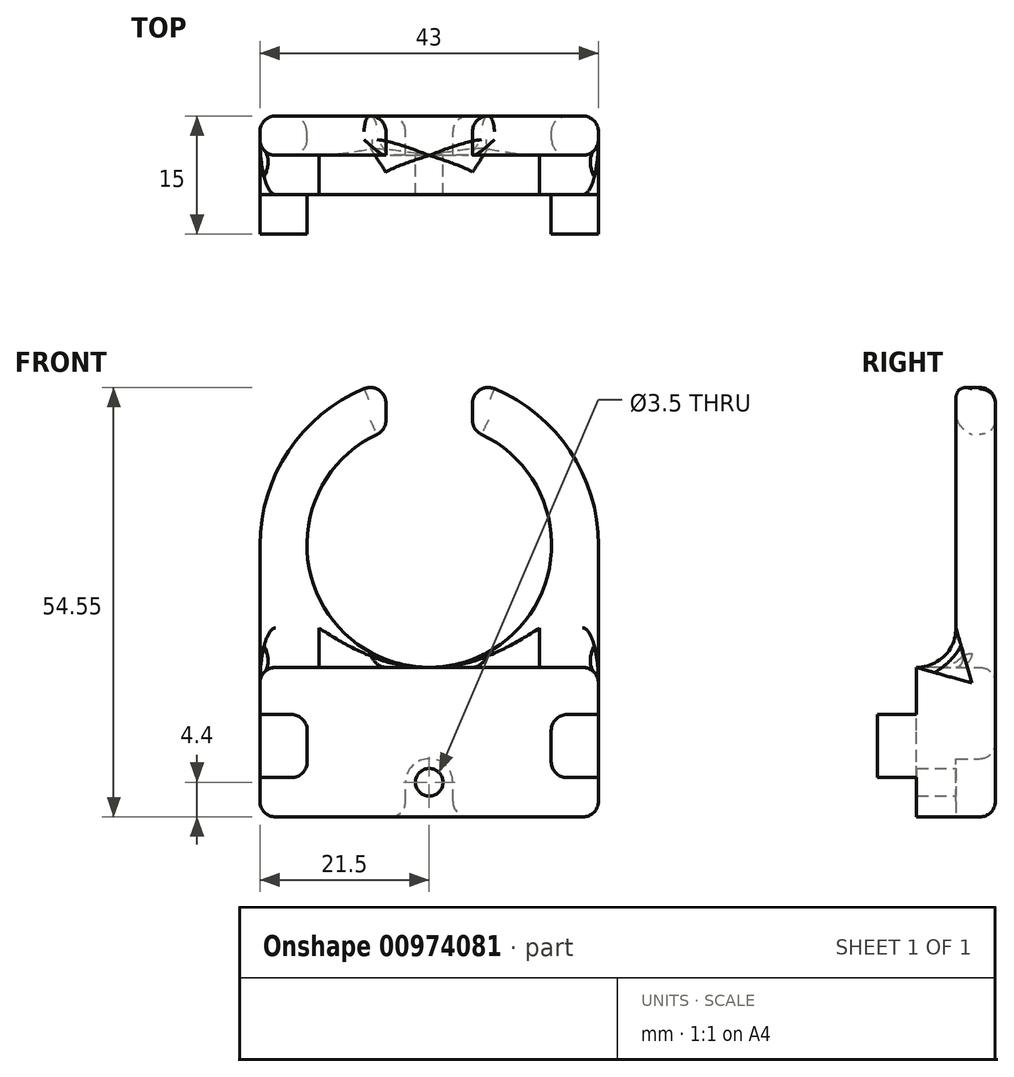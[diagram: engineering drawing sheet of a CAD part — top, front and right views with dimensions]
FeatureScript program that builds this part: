
annotation { "Feature Type Name" : "Feature", "Feature Type Description" : "" }
export const myFeature = defineFeature(function(context is Context, id is Id, definition is map)
    precondition{}
    {
        {
            var Q0;
            Q0=qCreatedBy(makeId("Front.planeOp"),FACE);
            var sketch = newSketch(context, id + "F0", { "sketchPlane" : qUnion([Q0])});
            skLineSegment(sketch, "E0.bottom", {"start": v(0, 0) * mm, "end": v(-43, 0) * mm});
            skLineSegment(sketch, "E0.top", {"start": v(0, 19) * mm, "end": v(-43, 19) * mm, "construction": true});
            skLineSegment(sketch, "E0.left", {"start": v(0, 0) * mm, "end": v(0, 19) * mm});
            skLineSegment(sketch, "E0.right", {"start": v(-43, 0) * mm, "end": v(-43, 19) * mm});
            skArc(sketch, "E1", {"start": v(0, 34.55) * mm, "mid": v(-21.5, 56.05) * mm, "end": v(-43, 34.55) * mm});
            skCircle(sketch, "E2", {"center": v(-21.5, 34.55) * mm, "radius": 15.55 * mm});
            skLineSegment(sketch, "E3", {"start": v(-43, 19) * mm, "end": v(-43, 34.55) * mm});
            skLineSegment(sketch, "E4", {"start": v(0, 19) * mm, "end": v(0, 34.55) * mm});
            skSolve(sketch);
        }
        {
            var Q0;
            Q0 = qSketchRegion(id + "F0", true);
            extrude(context, id + "F1", {"entities" : qUnion([Q0]), "depth" : 5 * mm, "offsetDistance" : 25 * mm});
        }
        {
            var Q0;
            Q0=makeQuery(id+"F1.opExtrude","CAP_FACE",FACE,{"disambiguationData":[OSD([sQuery(id+"F0.wireOp",EDGE,"E0.bottom"),sQuery(id+"F0.wireOp",EDGE,"E0.left"),sQuery(id+"F0.wireOp",EDGE,"E0.right"),sQuery(id+"F0.wireOp",EDGE,"E1"),sQuery(id+"F0.wireOp",EDGE,"E2"),sQuery(id+"F0.wireOp",EDGE,"E3"),sQuery(id+"F0.wireOp",EDGE,"E4")])],"isStart":false});
            var sketch = newSketch(context, id + "F2", { "sketchPlane" : qUnion([Q0])});
            skLineSegment(sketch, "E5.bottom", {"start": v(0, 0) * mm, "end": v(-43, 0) * mm});
            skLineSegment(sketch, "E5.top", {"start": v(0, 19) * mm, "end": v(-43, 19) * mm});
            skLineSegment(sketch, "E5.left", {"start": v(0, 0) * mm, "end": v(0, 19) * mm});
            skLineSegment(sketch, "E5.right", {"start": v(-43, 0) * mm, "end": v(-43, 19) * mm});
            skSolve(sketch);
        }
        {
            var Q0;
            {var subQ0=makeQuery(id+"F1.opExtrude","CAP_EDGE",EDGE,{"disambiguationData":[OSD([sQuery(id+"F0.wireOp",EDGE,"E1")])],"isStart":false});Q0=makeQuery(id+"F2.imprint","IMPRINT",FACE,{"disambiguationData":[TD([[makeQuery(id+"F2.imprint","IMPRINT",EDGE,{"derivedFrom":subQ0}),1.0]])]});}
            var sketch = newSketch(context, id + "F3", { "sketchPlane" : qUnion([Q0])});
            skLineSegment(sketch, "E6", {"start": v(-21.5, 34.05) * mm, "end": v(-21.5, 59.05) * mm, "construction": true});
            skLineSegment(sketch, "E7.bottom", {"start": v(-27, 59.05) * mm, "end": v(-16, 59.05) * mm});
            skLineSegment(sketch, "E7.top", {"start": v(-27, 47.05) * mm, "end": v(-16, 47.05) * mm});
            skLineSegment(sketch, "E7.left", {"start": v(-27, 59.05) * mm, "end": v(-27, 47.05) * mm});
            skLineSegment(sketch, "E7.right", {"start": v(-16, 59.05) * mm, "end": v(-16, 47.05) * mm});
            skSolve(sketch);
        }
        {
            var Q0;
            Q0 = qSketchRegion(id + "F3", true);
            var Q1;
            Q1=makeQuery(id+"F1.opExtrude","CAP_FACE",FACE,{"disambiguationData":[OSD([sQuery(id+"F0.wireOp",EDGE,"E0.bottom"),sQuery(id+"F0.wireOp",EDGE,"E0.left"),sQuery(id+"F0.wireOp",EDGE,"E0.right"),sQuery(id+"F0.wireOp",EDGE,"E1"),sQuery(id+"F0.wireOp",EDGE,"E2"),sQuery(id+"F0.wireOp",EDGE,"E3"),sQuery(id+"F0.wireOp",EDGE,"E4")])],"isStart":true});
            extrude(context, id + "F4", {"entities" : qUnion([Q0]), "operationType" : NewBodyOperationType.REMOVE, "endBound" : BoundingType.UP_TO_SURFACE, "oppositeDirection" : true, "depth" : 25 * mm, "endBoundEntityFace" : qUnion([Q1]), "offsetDistance" : 25 * mm});
        }
        {
            var Q0;
            Q0 = qSketchRegion(id + "F2", true);
            extrude(context, id + "F5", {"entities" : qUnion([Q0]), "operationType" : NewBodyOperationType.ADD, "depth" : 5 * mm, "offsetDistance" : 25 * mm});
        }
        {
            var Q0;
            Q0=makeQuery(id+"F5.opExtrude","CAP_FACE",FACE,{"disambiguationData":[OSD([sQuery(id+"F2.wireOp",EDGE,"E5.bottom"),sQuery(id+"F2.wireOp",EDGE,"E5.top"),sQuery(id+"F2.wireOp",EDGE,"E5.left"),sQuery(id+"F2.wireOp",EDGE,"E5.right")])],"isStart":false});
            var sketch = newSketch(context, id + "F6", { "sketchPlane" : qUnion([Q0])});
            skLineSegment(sketch, "E8.bottom", {"start": v(-43, 5) * mm, "end": v(-37, 5) * mm});
            skLineSegment(sketch, "E8.top", {"start": v(-43, 13) * mm, "end": v(-37, 13) * mm});
            skLineSegment(sketch, "E8.left", {"start": v(-43, 5) * mm, "end": v(-43, 13) * mm});
            skLineSegment(sketch, "E8.right", {"start": v(-37, 5) * mm, "end": v(-37, 13) * mm});
            skLineSegment(sketch, "E9.bottom", {"start": v(0, 13) * mm, "end": v(-6, 13) * mm});
            skLineSegment(sketch, "E9.top", {"start": v(0, 5) * mm, "end": v(-6, 5) * mm});
            skLineSegment(sketch, "E9.left", {"start": v(0, 13) * mm, "end": v(0, 5) * mm});
            skLineSegment(sketch, "E9.right", {"start": v(-6, 13) * mm, "end": v(-6, 5) * mm});
            skSolve(sketch);
        }
        {
            var Q0;
            Q0 = qSketchRegion(id + "F6", true);
            extrude(context, id + "F7", {"entities" : qUnion([Q0]), "operationType" : NewBodyOperationType.ADD, "depth" : 5 * mm, "offsetDistance" : 25 * mm});
        }
        {
            var Q0;
            Q0=makeQuery(id+"F1.opExtrude","CAP_EDGE",EDGE,{"disambiguationData":[OSD([sQuery(id+"F0.wireOp",EDGE,"E0.left"),sQuery(id+"F0.wireOp",EDGE,"E4")])],"isStart":false});
            var Q1;
            Q1=makeQuery(id+"F1.opExtrude","CAP_EDGE",EDGE,{"disambiguationData":[OSD([sQuery(id+"F0.wireOp",EDGE,"E2")])],"isStart":false});
            var Q2;
            Q2=makeQuery(id+"F1.opExtrude","CAP_EDGE",EDGE,{"disambiguationData":[OSD([sQuery(id+"F0.wireOp",EDGE,"E2")])],"isStart":true});
            var Q3;
            Q3=makeQuery(id+"F1.opExtrude","CAP_EDGE",EDGE,{"disambiguationData":[OSD([sQuery(id+"F0.wireOp",EDGE,"E0.left"),sQuery(id+"F0.wireOp",EDGE,"E4")])],"isStart":true});
            var Q4;
            Q4=makeQuery(id+"F1.opExtrude","CAP_EDGE",EDGE,{"disambiguationData":[OSD([sQuery(id+"F0.wireOp",EDGE,"E0.bottom")])],"isStart":true});
            var Q5;
            Q5=makeQuery(id+"F5.boolean.opBoolean","MERGE",EDGE,{"derivedFrom":[makeQuery(id+"F1.opExtrude","SWEPT_EDGE",EDGE,{"disambiguationData":[OSD([sQuery(id+"F0.wireOp",EDGE,"E0.bottom"),sQuery(id+"F0.wireOp",EDGE,"E0.left")])]}),makeQuery(id+"F5.opExtrude","SWEPT_EDGE",EDGE,{"disambiguationData":[OSD([sQuery(id+"F2.wireOp",EDGE,"E5.bottom"),sQuery(id+"F2.wireOp",EDGE,"E5.left")])]})]});
            var Q6;
            Q6=makeQuery(id+"F5.boolean.opBoolean","MERGE",EDGE,{"derivedFrom":[makeQuery(id+"F1.opExtrude","SWEPT_EDGE",EDGE,{"disambiguationData":[OSD([sQuery(id+"F0.wireOp",EDGE,"E0.bottom"),sQuery(id+"F0.wireOp",EDGE,"E0.right")])]}),makeQuery(id+"F5.opExtrude","SWEPT_EDGE",EDGE,{"disambiguationData":[OSD([sQuery(id+"F2.wireOp",EDGE,"E5.bottom"),sQuery(id+"F2.wireOp",EDGE,"E5.right")])]})]});
            var Q7;
            Q7=makeQuery(id+"F5.opExtrude","SWEPT_EDGE",EDGE,{"disambiguationData":[OSD([sQuery(id+"F0.wireOp",EDGE,"E0.right"),sQuery(id+"F0.wireOp",EDGE,"E3"),sQuery(id+"F2.wireOp",EDGE,"E5.top"),sQuery(id+"F2.wireOp",EDGE,"E5.right")])]});
            var Q8;
            Q8=makeQuery(id+"F5.opExtrude","SWEPT_EDGE",EDGE,{"disambiguationData":[OSD([sQuery(id+"F0.wireOp",EDGE,"E0.left"),sQuery(id+"F0.wireOp",EDGE,"E4"),sQuery(id+"F2.wireOp",EDGE,"E5.top"),sQuery(id+"F2.wireOp",EDGE,"E5.left")])]});
            var Q9;
            Q9=makeQuery(id+"F4.boolean.opBoolean","INTERSECT",EDGE,{"derivedFrom":[makeQuery(id+"F1.opExtrude","SWEPT_FACE",FACE,{"disambiguationData":[OSD([sQuery(id+"F0.wireOp",EDGE,"E1")])]}),makeQuery(id+"F4.opExtrude","SWEPT_FACE",FACE,{"disambiguationData":[OSD([sQuery(id+"F3.wireOp",EDGE,"E7.left")])]})]});
            var Q10;
            {var subQ1=sQuery(id+"F0.wireOp",EDGE,"E1");Q10=makeQuery(id+"F4.boolean.opBoolean","SPLIT",EDGE,{"disambiguationData":[TD([makeQuery(id+"F4.opExtrude","SWEPT_FACE",FACE,{"disambiguationData":[OSD([sQuery(id+"F3.wireOp",EDGE,"E7.left")])]})])],"derivedFrom":makeQuery(id+"F1.opExtrude","CAP_EDGE",EDGE,{"disambiguationData":[OSD([subQ1])],"isStart":false})});}
            var Q11;
            {var subQ1=sQuery(id+"F0.wireOp",EDGE,"E1");Q11=makeQuery(id+"F4.boolean.opBoolean","SPLIT",EDGE,{"disambiguationData":[TD([makeQuery(id+"F4.opExtrude","SWEPT_FACE",FACE,{"disambiguationData":[OSD([sQuery(id+"F3.wireOp",EDGE,"E7.left")])]})])],"derivedFrom":makeQuery(id+"F1.opExtrude","CAP_EDGE",EDGE,{"disambiguationData":[OSD([subQ1])],"isStart":true})});}
            var Q12;
            Q12=makeQuery(id+"F4.boolean.opBoolean","INTERSECT",EDGE,{"derivedFrom":[makeQuery(id+"F1.opExtrude","SWEPT_FACE",FACE,{"disambiguationData":[OSD([sQuery(id+"F0.wireOp",EDGE,"E2")])]}),makeQuery(id+"F4.opExtrude","SWEPT_FACE",FACE,{"disambiguationData":[OSD([sQuery(id+"F3.wireOp",EDGE,"E7.left")])]})]});
            var Q13;
            Q13=makeQuery(id+"F4.boolean.opBoolean","COPY",EDGE,{"derivedFrom":makeQuery(id+"F4.opExtrude","CAP_EDGE",EDGE,{"disambiguationData":[OSD([sQuery(id+"F3.wireOp",EDGE,"E7.left")])],"isStart":true})});
            var Q14;
            Q14=makeQuery(id+"F4.boolean.opBoolean","COPY",EDGE,{"derivedFrom":makeQuery(id+"F4.opExtrude","CAP_EDGE",EDGE,{"disambiguationData":[OSD([sQuery(id+"F3.wireOp",EDGE,"E7.left")])],"isStart":false})});
            var Q15;
            Q15=makeQuery(id+"F4.boolean.opBoolean","COPY",EDGE,{"derivedFrom":makeQuery(id+"F4.opExtrude","CAP_EDGE",EDGE,{"disambiguationData":[OSD([sQuery(id+"F3.wireOp",EDGE,"E7.right")])],"isStart":true})});
            var Q16;
            Q16=makeQuery(id+"F4.boolean.opBoolean","INTERSECT",EDGE,{"derivedFrom":[makeQuery(id+"F1.opExtrude","SWEPT_FACE",FACE,{"disambiguationData":[OSD([sQuery(id+"F0.wireOp",EDGE,"E2")])]}),makeQuery(id+"F4.opExtrude","SWEPT_FACE",FACE,{"disambiguationData":[OSD([sQuery(id+"F3.wireOp",EDGE,"E7.right")])]})]});
            var Q17;
            Q17=makeQuery(id+"F4.boolean.opBoolean","COPY",EDGE,{"derivedFrom":makeQuery(id+"F4.opExtrude","CAP_EDGE",EDGE,{"disambiguationData":[OSD([sQuery(id+"F3.wireOp",EDGE,"E7.right")])],"isStart":false})});
            var Q18;
            Q18=makeQuery(id+"F4.boolean.opBoolean","INTERSECT",EDGE,{"derivedFrom":[makeQuery(id+"F1.opExtrude","SWEPT_FACE",FACE,{"disambiguationData":[OSD([sQuery(id+"F0.wireOp",EDGE,"E1")])]}),makeQuery(id+"F4.opExtrude","SWEPT_FACE",FACE,{"disambiguationData":[OSD([sQuery(id+"F3.wireOp",EDGE,"E7.right")])]})]});
            fillet(context, id + "F8", {"entities" : qUnion([Q0, Q1, Q2, Q3, Q4, Q5, Q6, Q7, Q8, Q9, Q10, Q11, Q12, Q13, Q14, Q15, Q16, Q17, Q18]), "radius" : 2 * mm, "tangentPropagation" : true, "allowEdgeOverflow" : false});
        }
        {
            var Q0;
            {var subQ0=sQuery(id+"F2.wireOp",EDGE,"E5.top");Q0=makeQuery(id+"F5.boolean.opBoolean","SPLIT",EDGE,{"disambiguationData":[TD([makeQuery(id+"F5.opExtrude","SWEPT_FACE",FACE,{"disambiguationData":[OSD([sQuery(id+"F2.wireOp",EDGE,"E5.left")])]})])],"derivedFrom":makeQuery(id+"F5.opExtrude","CAP_EDGE",EDGE,{"disambiguationData":[OSD([subQ0])],"isStart":true})});}
            var Q1;
            {var subQ0=sQuery(id+"F2.wireOp",EDGE,"E5.top");Q1=makeQuery(id+"F5.boolean.opBoolean","SPLIT",EDGE,{"disambiguationData":[TD([makeQuery(id+"F5.opExtrude","SWEPT_FACE",FACE,{"disambiguationData":[OSD([sQuery(id+"F2.wireOp",EDGE,"E5.right")])]})])],"derivedFrom":makeQuery(id+"F5.opExtrude","CAP_EDGE",EDGE,{"disambiguationData":[OSD([subQ0])],"isStart":true})});}
            fillet(context, id + "F9", {"entities" : qUnion([Q0, Q1]), "radius" : 5 * mm, "tangentPropagation" : true, "allowEdgeOverflow" : false});
        }
        {
            var Q0;
            Q0=makeQuery(id+"F1.opExtrude","CAP_FACE",FACE,{"disambiguationData":[OSD([sQuery(id+"F0.wireOp",EDGE,"E0.bottom"),sQuery(id+"F0.wireOp",EDGE,"E0.left"),sQuery(id+"F0.wireOp",EDGE,"E0.right"),sQuery(id+"F0.wireOp",EDGE,"E1"),sQuery(id+"F0.wireOp",EDGE,"E2"),sQuery(id+"F0.wireOp",EDGE,"E3"),sQuery(id+"F0.wireOp",EDGE,"E4")])],"isStart":true});
            var sketch = newSketch(context, id + "F10", { "sketchPlane" : qUnion([Q0])});
            skCircle(sketch, "E10", {"center": v(21.5, 4.4) * mm, "radius": 1.75 * mm});
            skLineSegment(sketch, "E11", {"start": v(21.5, 2) * mm, "end": v(21.5, 32.35) * mm, "construction": true});
            skSolve(sketch);
        }
        {
            var Q0;
            Q0 = qSketchRegion(id + "F10", true);
            var Q1;
            Q1=makeQuery(id+"F5.opExtrude","CAP_FACE",FACE,{"disambiguationData":[OSD([sQuery(id+"F2.wireOp",EDGE,"E5.bottom"),sQuery(id+"F2.wireOp",EDGE,"E5.top"),sQuery(id+"F2.wireOp",EDGE,"E5.left"),sQuery(id+"F2.wireOp",EDGE,"E5.right")])],"isStart":false});
            extrude(context, id + "F11", {"entities" : qUnion([Q0]), "operationType" : NewBodyOperationType.REMOVE, "endBound" : BoundingType.UP_TO_SURFACE, "oppositeDirection" : true, "depth" : 25 * mm, "endBoundEntityFace" : qUnion([Q1]), "offsetDistance" : 25 * mm});
        }
        {
            var Q0;
            Q0=makeQuery(id+"F1.opExtrude","CAP_FACE",FACE,{"disambiguationData":[OSD([sQuery(id+"F0.wireOp",EDGE,"E0.bottom"),sQuery(id+"F0.wireOp",EDGE,"E0.left"),sQuery(id+"F0.wireOp",EDGE,"E0.right"),sQuery(id+"F0.wireOp",EDGE,"E1"),sQuery(id+"F0.wireOp",EDGE,"E2"),sQuery(id+"F0.wireOp",EDGE,"E3"),sQuery(id+"F0.wireOp",EDGE,"E4")])],"isStart":true});
            var sketch = newSketch(context, id + "F12", { "sketchPlane" : qUnion([Q0])});
            skLineSegment(sketch, "E12", {"start": v(21.5, -3.6) * mm, "end": v(21.5, 4.4) * mm});
            skPoint(sketch, "E12.startSnap0", {"position": v(21.5, 2) * mm});
            skArc(sketch, "E13.0.startCap", {"start": v(24.5, -3.6) * mm, "mid": v(21.5, -6.6) * mm, "end": v(18.5, -3.6) * mm});
            skArc(sketch, "E13.0.endCap", {"start": v(18.5, 4.4) * mm, "mid": v(21.5, 7.4) * mm, "end": v(24.5, 4.4) * mm});
            skLineSegment(sketch, "E13.0.left", {"start": v(18.5, -3.6) * mm, "end": v(18.5, 4.4) * mm});
            skLineSegment(sketch, "E13.0.right", {"start": v(24.5, -3.6) * mm, "end": v(24.5, 4.4) * mm});
            skSolve(sketch);
        }
        {
            var Q0;
            Q0 = qSketchRegion(id + "F12", true);
            extrude(context, id + "F13", {"entities" : qUnion([Q0]), "operationType" : NewBodyOperationType.REMOVE, "oppositeDirection" : true, "depth" : 5 * mm, "offsetDistance" : 25 * mm});
        }
        {
            var Q0;
            Q0=makeQuery(id+"F1.opExtrude","CAP_FACE",FACE,{"disambiguationData":[OSD([sQuery(id+"F0.wireOp",EDGE,"E0.bottom"),sQuery(id+"F0.wireOp",EDGE,"E0.left"),sQuery(id+"F0.wireOp",EDGE,"E0.right"),sQuery(id+"F0.wireOp",EDGE,"E1"),sQuery(id+"F0.wireOp",EDGE,"E2"),sQuery(id+"F0.wireOp",EDGE,"E3"),sQuery(id+"F0.wireOp",EDGE,"E4")])],"isStart":true});
            var Q1;
            Q1=makeQuery(id+"F13.boolean.opBoolean","COPY",EDGE,{"derivedFrom":makeQuery(id+"F13.opExtrude","CAP_EDGE",EDGE,{"disambiguationData":[OSD([sQuery(id+"F12.wireOp",EDGE,"E13.0.right")])],"isStart":true})});
            var Q2;
            Q2=makeQuery(id+"F7.opExtrude","SWEPT_EDGE",EDGE,{"disambiguationData":[OSD([sQuery(id+"F6.wireOp",EDGE,"E9.top"),sQuery(id+"F6.wireOp",EDGE,"E9.right")])]});
            var Q3;
            Q3=makeQuery(id+"F7.opExtrude","SWEPT_EDGE",EDGE,{"disambiguationData":[OSD([sQuery(id+"F6.wireOp",EDGE,"E9.bottom"),sQuery(id+"F6.wireOp",EDGE,"E9.right")])]});
            var Q4;
            Q4=makeQuery(id+"F7.opExtrude","SWEPT_EDGE",EDGE,{"disambiguationData":[OSD([sQuery(id+"F6.wireOp",EDGE,"E8.bottom"),sQuery(id+"F6.wireOp",EDGE,"E8.right")])]});
            var Q5;
            Q5=makeQuery(id+"F7.opExtrude","SWEPT_EDGE",EDGE,{"disambiguationData":[OSD([sQuery(id+"F6.wireOp",EDGE,"E8.top"),sQuery(id+"F6.wireOp",EDGE,"E8.right")])]});
            fillet(context, id + "F14", {"entities" : qUnion([Q0, Q1, Q2, Q3, Q4, Q5]), "radius" : 2 * mm, "tangentPropagation" : true, "allowEdgeOverflow" : false});
        }
    });
